# Revit family: streetlight_sl_31_micro___p0_5a_5xh5v31t08ca_819b
name_source: partatom
category: Lighting Fixtures
units: mm (PartAtom-declared; Revit-internal decimal feet)

## family parameters
Cut with Voids When Loaded = No
Host = Face
Light Source = No
Part Type = Normal
Room Calculation Point = No
Round Connector Dimension = Use Diameter
Shared = No

## types (1)
- --- (1 x LED, 1420 lm, 10.2 W, 3000K)
    Apparent Load = 10 VA
    CIE Flux Codes = 37 73 96 100 100
    Color Rendering = 70
    Color Temperature = 3000K
    Default Elevation = 1800 mm
    Description = Streetlight SL 31 micro D4i, Desk-Remote mast luminaire for post-top, side-entry; light control with lens of PMMA; light distribution: P0.5a, direct asymmetric distribution, for standard-compliant lighting for roads and squares; LED: luminous flux: 1.420lm, light colour: 730, colour temperature: 3000K; luminous efficacy: 139,2lm/W; control: pre-setting: logarithmic dimming characteristic, flexible luminous flux parameterisation, time-dependent luminous flux control, constant luminous flux control, power reduction, intelligent temperature release in ECG and LED module, overheat protection; luminaire housing, of diecast aluminium, SITECO metallic grey (DB 702S), corrosivity category C5 high according to DIN EN ISO 12944; cover of toughened safety glass, transparent, opened without tools; mast flange of diecast aluminium, SITECO metallic grey (DB 702S), spigot size: 76/60mm, mast flange included unmounted; with cable H07RN-F 2x 1.5mm², cable length: 5,5m, connection cable pre-assembled; mains connection: 220..240V, AC, 50/60Hz; power consumption (at start of service life): 10,2W / (at end of service life): 10,5W / (with reduced operation 50%): 5,3W; protection rating (complete): IP66; insulation class (complete): insulation class II (safety insulation); impact resistance: IK09; certification: CE, ENEC, ENEC+, VDE, UKCA, ZD4i; permissible operating ambient temperature for outdoor applications: -40..+50°C; packaging unit: 1 piece

Light Distribution: P0.5a
    Height = 76 mm
    Lamp = 1 x LED
    Lamp Light Flux = 1420 lm
    Lamp Power = 10.2 W
    Lamp count = 1
    Length = 467 mm
    Luminous efficacy = 139 lm/W
    Manufacturer = Siteco
    ModVariant = No
    Model = 5XH5V31T08CA
    Number of Poles = 1
    OnlyDefault = Yes
    Power Factor = 1
    Product Name = Streetlight SL 31 micro | P0.5a
    Product group = mast luminaire | pylon top
    ProductGroupID = 6100
    Protection Class = Protection class II
    Protection Degree = IP 66
    RLX_Detail_Level = 1
    RLX_Emergency_Light_Flux = 0 lm
    RLX_Emergency_Type = 0
    RLX_Emergency_Type_DB = No
    RlxData = <blob elided: 43769 chars, md5=b0ff0b66>
    Socket = socket
    Standby Power = 0 W
    System Light Flux = 1420 lm
    System Power = 10 W
    Type Comments = factory setting: luminous flux: 100 % | dim-lin: 254 | 386 mA
    Type Image = l_1300315.jpg
    URL = http://relux.com
    VarID = @adj_055853
    Voltage = 0 V
    Weight = 0.00 kg
    Width = 265 mm

## geometry (parser evidence)
native form markers: Sweep x8
no freeform markers — native parametric forms only
